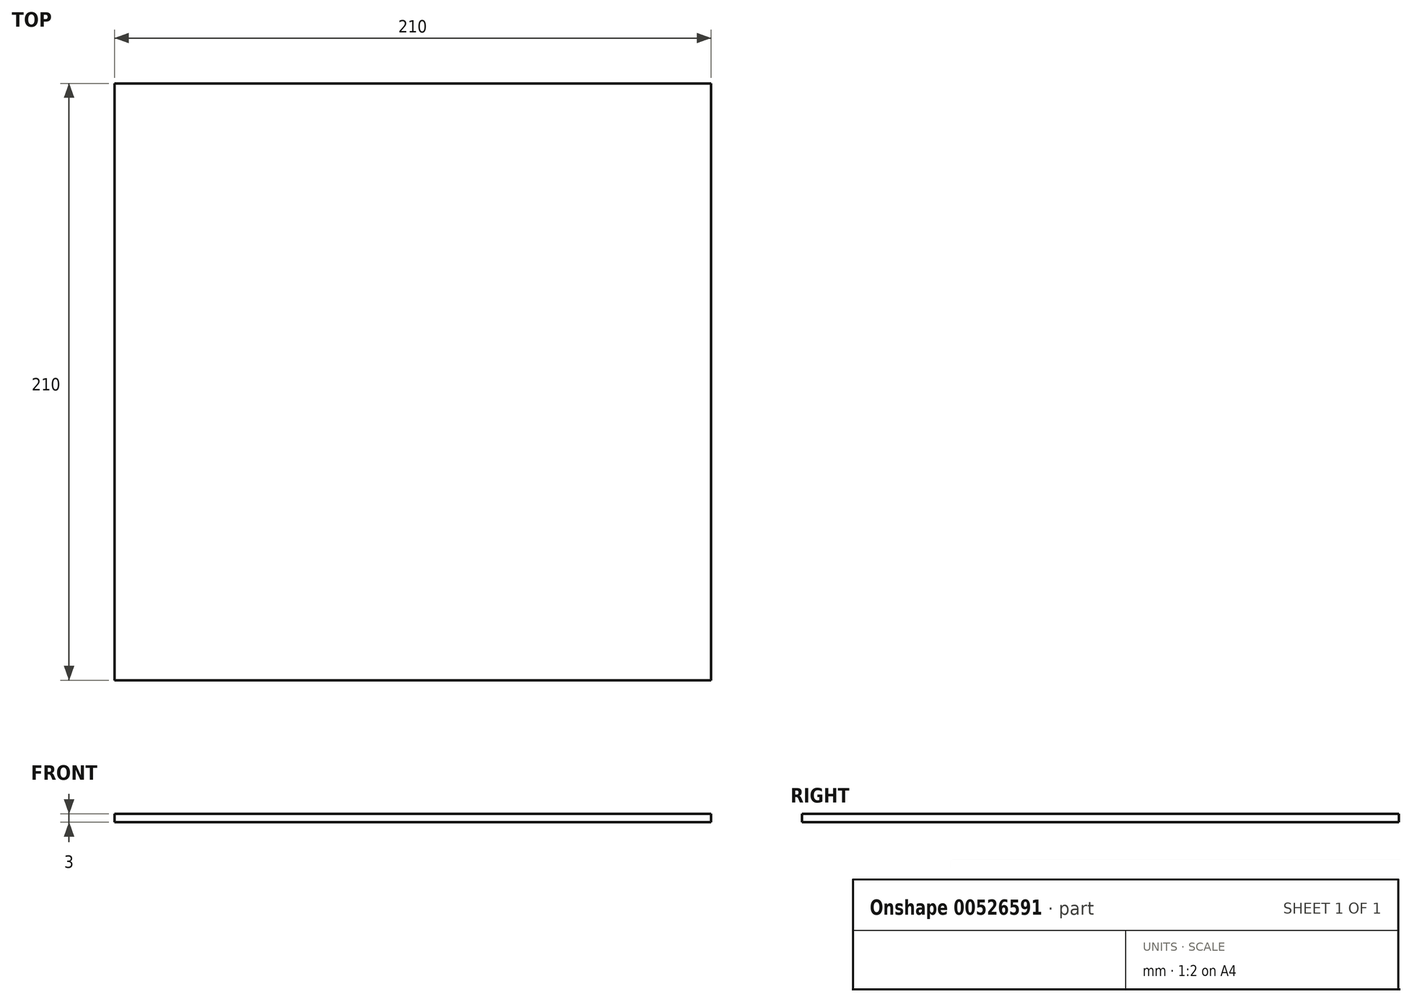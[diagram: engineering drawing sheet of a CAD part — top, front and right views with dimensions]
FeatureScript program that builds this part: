
annotation { "Feature Type Name" : "Feature", "Feature Type Description" : "" }
export const myFeature = defineFeature(function(context is Context, id is Id, definition is map)
    precondition{}
    {
        {
            var Q0;
            Q0=qCreatedBy(makeId("Top.planeOp"),FACE);
            var sketch = newSketch(context, id + "F0", { "sketchPlane" : qUnion([Q0])});
            skLineSegment(sketch, "E0.bottom", {"start": v(-99.88, -65.08) * mm, "end": v(110.12, -65.08) * mm});
            skLineSegment(sketch, "E0.top", {"start": v(-99.88, 144.92) * mm, "end": v(110.12, 144.92) * mm});
            skLineSegment(sketch, "E0.left", {"start": v(-99.88, -65.08) * mm, "end": v(-99.88, 144.92) * mm});
            skLineSegment(sketch, "E0.right", {"start": v(110.12, -65.08) * mm, "end": v(110.12, 144.92) * mm});
            skSolve(sketch);
        }
        {
            var Q0;
            Q0 = qSketchRegion(id + "F0", true);
            extrude(context, id + "F1", {"entities" : qUnion([Q0]), "depth" : 3 * mm, "offsetDistance" : 25 * mm});
        }
    });
